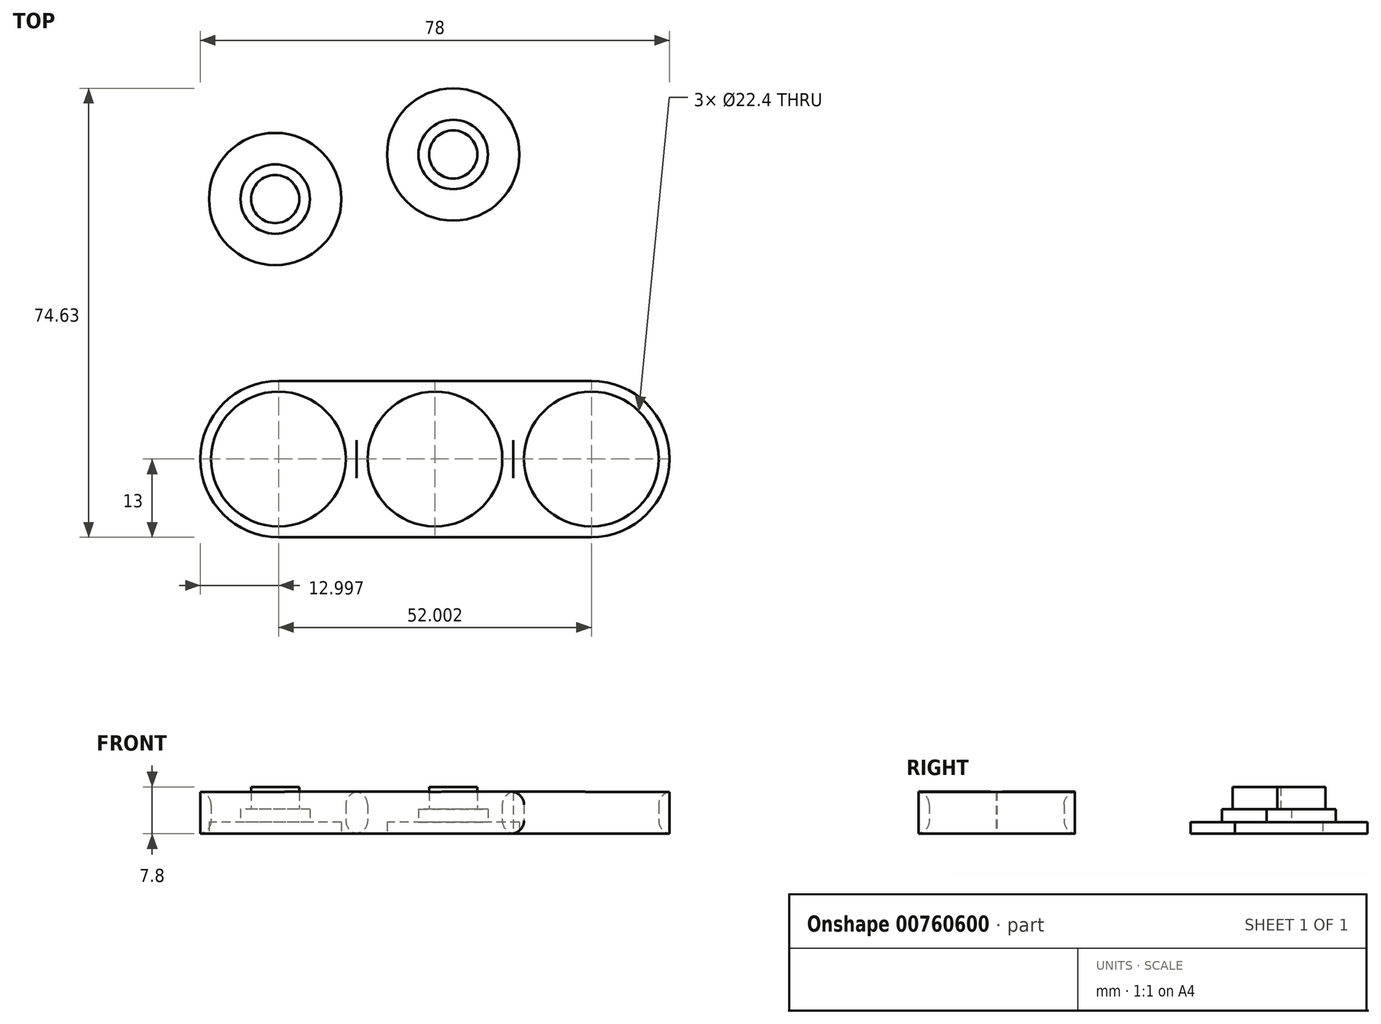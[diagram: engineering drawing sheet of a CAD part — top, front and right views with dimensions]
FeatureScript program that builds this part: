
annotation { "Feature Type Name" : "Feature", "Feature Type Description" : "" }
export const myFeature = defineFeature(function(context is Context, id is Id, definition is map)
    precondition{}
    {
        {
            var Q0;
            Q0=qCreatedBy(makeId("Top.planeOp"),FACE);
            var sketch = newSketch(context, id + "F0", { "sketchPlane" : qUnion([Q0])});
            skCircle(sketch, "E0", {"center": v(0, 0) * mm, "radius": 11.2 * mm});
            skCircle(sketch, "E1", {"center": v(0, 0) * mm, "radius": 13 * mm});
            skCircle(sketch, "E2", {"center": v(26, 0) * mm, "radius": 13 * mm});
            skCircle(sketch, "E3", {"center": v(26, 0) * mm, "radius": 11.2 * mm});
            skCircle(sketch, "E4", {"center": v(-26, 0) * mm, "radius": 13 * mm});
            skCircle(sketch, "E5", {"center": v(-26, 0) * mm, "radius": 11.2 * mm});
            skLineSegment(sketch, "E6", {"start": v(-26, 13) * mm, "end": v(26, 13) * mm});
            skLineSegment(sketch, "E7", {"start": v(26, 0) * mm, "end": v(26, -15.13) * mm, "construction": true});
            skLineSegment(sketch, "E8", {"start": v(26, -13) * mm, "end": v(-26, -13) * mm});
            skSolve(sketch);
        }
        {
            var Q0;
            Q0 = qSketchRegion(id + "F0", true);
            extrude(context, id + "F1", {"entities" : qUnion([Q0]), "depth" : 7 * mm, "offsetDistance" : 25 * mm});
        }
        {
            var Q0;
            Q0=makeQuery(id+"F1.opExtrude","CAP_EDGE",EDGE,{"disambiguationData":[OSD([sQuery(id+"F0.wireOp",EDGE,"E5")])],"isStart":false});
            var Q1;
            Q1=makeQuery(id+"F1.opExtrude","CAP_EDGE",EDGE,{"disambiguationData":[OSD([sQuery(id+"F0.wireOp",EDGE,"E0")])],"isStart":false});
            var Q2;
            Q2=makeQuery(id+"F1.opExtrude","CAP_EDGE",EDGE,{"disambiguationData":[OSD([sQuery(id+"F0.wireOp",EDGE,"E3")])],"isStart":false});
            var Q3;
            Q3=makeQuery(id+"F1.opExtrude","CAP_EDGE",EDGE,{"disambiguationData":[OSD([sQuery(id+"F0.wireOp",EDGE,"E0")])],"isStart":true});
            var Q4;
            Q4=makeQuery(id+"F1.opExtrude","CAP_EDGE",EDGE,{"disambiguationData":[OSD([sQuery(id+"F0.wireOp",EDGE,"E3")])],"isStart":true});
            var Q5;
            Q5=makeQuery(id+"F1.opExtrude","CAP_EDGE",EDGE,{"disambiguationData":[OSD([sQuery(id+"F0.wireOp",EDGE,"E5")])],"isStart":true});
            fillet(context, id + "F2", {"entities" : qUnion([Q0, Q1, Q2, Q3, Q4, Q5]), "radius" : 2.17 * mm, "tangentPropagation" : true, "allowEdgeOverflow" : false});
        }
        {
            var Q0;
            Q0=qCreatedBy(makeId("Top.planeOp"),FACE);
            var sketch = newSketch(context, id + "F3", { "sketchPlane" : qUnion([Q0])});
            skCircle(sketch, "E9", {"center": v(-26.56, 43.21) * mm, "radius": 11 * mm});
            skCircle(sketch, "E10.1.0", {"center": v(3.03, 50.63) * mm, "radius": 11 * mm});
            skPoint(sketch, "E10.center", {"position": v(0, 0) * mm});
            skLineSegment(sketch, "E10.anchor1", {"start": v(0, 0) * mm, "end": v(-26.56, 43.21) * mm, "construction": true});
            skLineSegment(sketch, "E10.anchor2", {"start": v(0, 0) * mm, "end": v(3.03, 50.63) * mm, "construction": true});
            skSolve(sketch);
        }
        {
            var Q0;
            Q0 = qSketchRegion(id + "F3", true);
            extrude(context, id + "F4", {"entities" : qUnion([Q0]), "depth" : 1.9 * mm, "offsetDistance" : 25 * mm});
        }
        {
            var Q0;
            Q0=makeQuery(id+"F4.opExtrude","CAP_FACE",FACE,{"disambiguationData":[OSD([sQuery(id+"F3.wireOp",EDGE,"E9")])],"isStart":false});
            var sketch = newSketch(context, id + "F5", { "sketchPlane" : qUnion([Q0])});
            skCircle(sketch, "E11", {"center": v(-26.56, 43.21) * mm, "radius": 5.77 * mm});
            skCircle(sketch, "E12.1.0", {"center": v(3.03, 50.63) * mm, "radius": 5.77 * mm});
            skPoint(sketch, "E12.center", {"position": v(0, 0) * mm});
            skLineSegment(sketch, "E12.anchor1", {"start": v(0, 0) * mm, "end": v(-26.56, 43.21) * mm, "construction": true});
            skLineSegment(sketch, "E12.anchor2", {"start": v(0, 0) * mm, "end": v(3.03, 50.63) * mm, "construction": true});
            skSolve(sketch);
        }
        {
            var Q0;
            Q0 = qSketchRegion(id + "F5", true);
            extrude(context, id + "F6", {"entities" : qUnion([Q0]), "operationType" : NewBodyOperationType.ADD, "depth" : 2.2 * mm, "offsetDistance" : 25 * mm});
        }
        {
            var Q0;
            Q0=makeQuery(id+"F6.opExtrude","CAP_FACE",FACE,{"disambiguationData":[OSD([sQuery(id+"F5.wireOp",EDGE,"E11")])],"isStart":false});
            var sketch = newSketch(context, id + "F7", { "sketchPlane" : qUnion([Q0])});
            skCircle(sketch, "E13", {"center": v(-26.56, 43.21) * mm, "radius": 4 * mm});
            skCircle(sketch, "E14.1.0", {"center": v(3.03, 50.63) * mm, "radius": 4 * mm});
            skPoint(sketch, "E14.center", {"position": v(0, 0) * mm});
            skLineSegment(sketch, "E14.anchor1", {"start": v(0, 0) * mm, "end": v(-26.56, 43.21) * mm, "construction": true});
            skLineSegment(sketch, "E14.anchor2", {"start": v(0, 0) * mm, "end": v(3.03, 50.63) * mm, "construction": true});
            skSolve(sketch);
        }
        {
            var Q0;
            Q0 = qSketchRegion(id + "F7", true);
            extrude(context, id + "F8", {"entities" : qUnion([Q0]), "operationType" : NewBodyOperationType.ADD, "depth" : 3.7 * mm, "offsetDistance" : 25 * mm});
        }
    });
